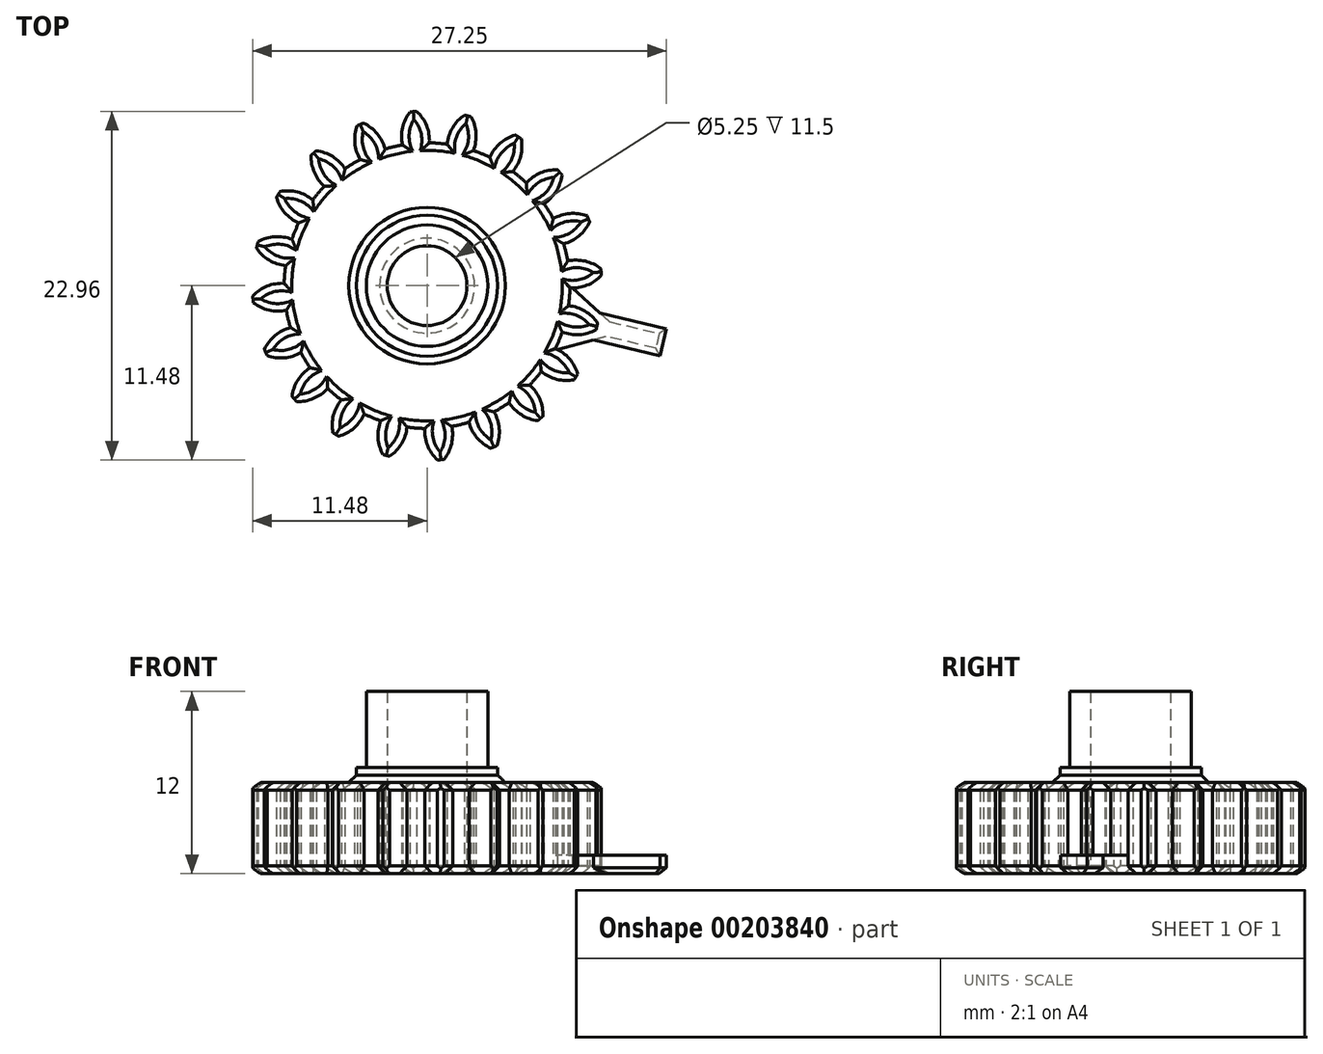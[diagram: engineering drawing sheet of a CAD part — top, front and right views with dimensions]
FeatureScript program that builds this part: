
annotation { "Feature Type Name" : "Feature", "Feature Type Description" : "" }
export const myFeature = defineFeature(function(context is Context, id is Id, definition is map)
    precondition{}
    {
        {
            assignVariable(context, id + "F0", {"name" : "GearDepth", "anyValue" : 6});
        }
        {
            var Q0;
            Q0=qCreatedBy(makeId("Top.planeOp"),FACE);
            var sketch = newSketch(context, id + "F1", { "sketchPlane" : qUnion([Q0])});
            skCircle(sketch, "E0", {"center": v(0, 0) * mm, "radius": 9.4 * mm});
            skCircle(sketch, "E1", {"center": v(0, 0) * mm, "radius": 10.45 * mm, "construction": true});
            skCircle(sketch, "E2", {"center": v(0, 0) * mm, "radius": 11.5 * mm, "construction": true});
            skLineSegment(sketch, "E3", {"start": v(0, 0) * mm, "end": v(0, 17.6) * mm, "construction": true});
            skLineSegment(sketch, "E4", {"start": v(0, 0) * mm, "end": v(-1.42, 18) * mm, "construction": true});
            skLineSegment(sketch, "E5", {"start": v(0, 10.45) * mm, "end": v(-10.54, 10.45) * mm, "construction": true});
            skLineSegment(sketch, "E6", {"start": v(0, 10.45) * mm, "end": v(-10.3, 6.7) * mm, "construction": true});
            skCircle(sketch, "E7", {"center": v(0, 10.45) * mm, "radius": 2.61 * mm, "construction": true});
            skCircle(sketch, "E8", {"center": v(-2.46, 9.56) * mm, "radius": 2.61 * mm, "construction": true});
            skArc(sketch, "E9", {"start": v(-4.91, 10.45) * mm, "mid": v(-4.92, 10.42) * mm, "end": v(-4.94, 10.39) * mm});
            skArc(sketch, "E10.trimOffspring", {"start": v(0.15, 9.4) * mm, "mid": v(-0.03, 10.54) * mm, "end": v(-0.68, 11.48) * mm});
            skArc(sketch, "E11.MirrorCS", {"start": v(-1.62, 9.27) * mm, "mid": v(-1.62, 10.41) * mm, "end": v(-1.12, 11.45) * mm});
            skLineSegment(sketch, "E12", {"start": v(-1.12, 11.45) * mm, "end": v(-0.68, 11.48) * mm});
            skArc(sketch, "E13.1.0", {"start": v(-2.76, 9) * mm, "mid": v(-3.29, 10.01) * mm, "end": v(-4.2, 10.7) * mm});
            skLineSegment(sketch, "E13.1.1", {"start": v(-4.6, 10.54) * mm, "end": v(-4.2, 10.7) * mm});
            skArc(sketch, "E13.1.2", {"start": v(-4.4, 8.31) * mm, "mid": v(-4.76, 9.4) * mm, "end": v(-4.6, 10.54) * mm});
            skArc(sketch, "E13.2.0", {"start": v(-5.4, 7.7) * mm, "mid": v(-6.22, 8.5) * mm, "end": v(-7.3, 8.89) * mm});
            skLineSegment(sketch, "E13.2.1", {"start": v(-7.64, 8.6) * mm, "end": v(-7.3, 8.89) * mm});
            skArc(sketch, "E13.2.2", {"start": v(-6.76, 6.54) * mm, "mid": v(-7.43, 7.47) * mm, "end": v(-7.64, 8.6) * mm});
            skArc(sketch, "E13.3.0", {"start": v(-7.52, 5.65) * mm, "mid": v(-8.54, 6.17) * mm, "end": v(-9.69, 6.2) * mm});
            skLineSegment(sketch, "E13.3.1", {"start": v(-9.92, 5.82) * mm, "end": v(-9.69, 6.2) * mm});
            skArc(sketch, "E13.3.2", {"start": v(-8.45, 4.13) * mm, "mid": v(-9.37, 4.81) * mm, "end": v(-9.92, 5.82) * mm});
            skArc(sketch, "E13.4.0", {"start": v(-8.9, 3.05) * mm, "mid": v(-10.03, 3.23) * mm, "end": v(-11.13, 2.9) * mm});
            skLineSegment(sketch, "E13.4.1", {"start": v(-11.23, 2.47) * mm, "end": v(-11.13, 2.9) * mm});
            skArc(sketch, "E13.4.2", {"start": v(-9.32, 1.32) * mm, "mid": v(-10.4, 1.68) * mm, "end": v(-11.23, 2.47) * mm});
            skArc(sketch, "E13.5.0", {"start": v(-9.4, 0.15) * mm, "mid": v(-10.54, -0.03) * mm, "end": v(-11.48, -0.68) * mm});
            skLineSegment(sketch, "E13.5.1", {"start": v(-11.45, -1.12) * mm, "end": v(-11.48, -0.68) * mm});
            skArc(sketch, "E13.5.2", {"start": v(-9.27, -1.62) * mm, "mid": v(-10.41, -1.62) * mm, "end": v(-11.45, -1.12) * mm});
            skArc(sketch, "E13.6.0", {"start": v(-9, -2.76) * mm, "mid": v(-10.01, -3.29) * mm, "end": v(-10.7, -4.2) * mm});
            skLineSegment(sketch, "E13.6.1", {"start": v(-10.54, -4.6) * mm, "end": v(-10.7, -4.2) * mm});
            skArc(sketch, "E13.6.2", {"start": v(-8.31, -4.4) * mm, "mid": v(-9.4, -4.76) * mm, "end": v(-10.54, -4.6) * mm});
            skArc(sketch, "E13.7.0", {"start": v(-7.7, -5.4) * mm, "mid": v(-8.5, -6.22) * mm, "end": v(-8.89, -7.3) * mm});
            skLineSegment(sketch, "E13.7.1", {"start": v(-8.6, -7.64) * mm, "end": v(-8.89, -7.3) * mm});
            skArc(sketch, "E13.7.2", {"start": v(-6.54, -6.76) * mm, "mid": v(-7.47, -7.43) * mm, "end": v(-8.6, -7.64) * mm});
            skArc(sketch, "E13.8.0", {"start": v(-5.65, -7.52) * mm, "mid": v(-6.17, -8.54) * mm, "end": v(-6.2, -9.69) * mm});
            skLineSegment(sketch, "E13.8.1", {"start": v(-5.82, -9.92) * mm, "end": v(-6.2, -9.69) * mm});
            skArc(sketch, "E13.8.2", {"start": v(-4.13, -8.45) * mm, "mid": v(-4.81, -9.37) * mm, "end": v(-5.82, -9.92) * mm});
            skArc(sketch, "E13.9.0", {"start": v(-3.05, -8.9) * mm, "mid": v(-3.23, -10.03) * mm, "end": v(-2.9, -11.13) * mm});
            skLineSegment(sketch, "E13.9.1", {"start": v(-2.47, -11.23) * mm, "end": v(-2.9, -11.13) * mm});
            skArc(sketch, "E13.9.2", {"start": v(-1.32, -9.32) * mm, "mid": v(-1.68, -10.4) * mm, "end": v(-2.47, -11.23) * mm});
            skArc(sketch, "E13.10.0", {"start": v(-0.15, -9.4) * mm, "mid": v(0.03, -10.54) * mm, "end": v(0.68, -11.48) * mm});
            skLineSegment(sketch, "E13.10.1", {"start": v(1.12, -11.45) * mm, "end": v(0.68, -11.48) * mm});
            skArc(sketch, "E13.10.2", {"start": v(1.62, -9.27) * mm, "mid": v(1.62, -10.41) * mm, "end": v(1.12, -11.45) * mm});
            skArc(sketch, "E13.11.0", {"start": v(2.76, -9) * mm, "mid": v(3.29, -10.01) * mm, "end": v(4.2, -10.7) * mm});
            skLineSegment(sketch, "E13.11.1", {"start": v(4.6, -10.54) * mm, "end": v(4.2, -10.7) * mm});
            skArc(sketch, "E13.11.2", {"start": v(4.4, -8.31) * mm, "mid": v(4.76, -9.4) * mm, "end": v(4.6, -10.54) * mm});
            skArc(sketch, "E13.12.0", {"start": v(5.4, -7.7) * mm, "mid": v(6.22, -8.5) * mm, "end": v(7.3, -8.89) * mm});
            skLineSegment(sketch, "E13.12.1", {"start": v(7.64, -8.6) * mm, "end": v(7.3, -8.89) * mm});
            skArc(sketch, "E13.12.2", {"start": v(6.76, -6.54) * mm, "mid": v(7.43, -7.47) * mm, "end": v(7.64, -8.6) * mm});
            skArc(sketch, "E13.13.0", {"start": v(7.52, -5.65) * mm, "mid": v(8.54, -6.17) * mm, "end": v(9.69, -6.2) * mm});
            skLineSegment(sketch, "E13.13.1", {"start": v(9.92, -5.82) * mm, "end": v(9.69, -6.2) * mm});
            skArc(sketch, "E13.13.2", {"start": v(8.45, -4.13) * mm, "mid": v(9.37, -4.81) * mm, "end": v(9.92, -5.82) * mm});
            skArc(sketch, "E13.14.0", {"start": v(8.9, -3.05) * mm, "mid": v(10.03, -3.23) * mm, "end": v(11.13, -2.9) * mm});
            skLineSegment(sketch, "E13.14.1", {"start": v(11.23, -2.47) * mm, "end": v(11.13, -2.9) * mm});
            skArc(sketch, "E13.14.2", {"start": v(9.32, -1.32) * mm, "mid": v(10.4, -1.68) * mm, "end": v(11.23, -2.47) * mm});
            skArc(sketch, "E13.15.0", {"start": v(9.4, -0.15) * mm, "mid": v(10.54, 0.03) * mm, "end": v(11.48, 0.68) * mm});
            skLineSegment(sketch, "E13.15.1", {"start": v(11.45, 1.12) * mm, "end": v(11.48, 0.68) * mm});
            skArc(sketch, "E13.15.2", {"start": v(9.27, 1.62) * mm, "mid": v(10.41, 1.62) * mm, "end": v(11.45, 1.12) * mm});
            skArc(sketch, "E13.16.0", {"start": v(9, 2.76) * mm, "mid": v(10.01, 3.29) * mm, "end": v(10.7, 4.2) * mm});
            skLineSegment(sketch, "E13.16.1", {"start": v(10.54, 4.6) * mm, "end": v(10.7, 4.2) * mm});
            skArc(sketch, "E13.16.2", {"start": v(8.31, 4.4) * mm, "mid": v(9.4, 4.76) * mm, "end": v(10.54, 4.6) * mm});
            skArc(sketch, "E13.17.0", {"start": v(7.7, 5.4) * mm, "mid": v(8.5, 6.22) * mm, "end": v(8.89, 7.3) * mm});
            skLineSegment(sketch, "E13.17.1", {"start": v(8.6, 7.64) * mm, "end": v(8.89, 7.3) * mm});
            skArc(sketch, "E13.17.2", {"start": v(6.54, 6.76) * mm, "mid": v(7.47, 7.43) * mm, "end": v(8.6, 7.64) * mm});
            skArc(sketch, "E13.18.0", {"start": v(5.65, 7.52) * mm, "mid": v(6.17, 8.54) * mm, "end": v(6.2, 9.69) * mm});
            skLineSegment(sketch, "E13.18.1", {"start": v(5.82, 9.92) * mm, "end": v(6.2, 9.69) * mm});
            skArc(sketch, "E13.18.2", {"start": v(4.13, 8.45) * mm, "mid": v(4.81, 9.37) * mm, "end": v(5.82, 9.92) * mm});
            skArc(sketch, "E13.19.0", {"start": v(3.05, 8.9) * mm, "mid": v(3.23, 10.03) * mm, "end": v(2.9, 11.13) * mm});
            skLineSegment(sketch, "E13.19.1", {"start": v(2.47, 11.23) * mm, "end": v(2.9, 11.13) * mm});
            skArc(sketch, "E13.19.2", {"start": v(1.32, 9.32) * mm, "mid": v(1.68, 10.4) * mm, "end": v(2.47, 11.23) * mm});
            skSolve(sketch);
        }
        {
            var Q0;
            {var subQ0=sQuery(id+"F1.wireOp",EDGE,"E10.trimOffspring");Q0=makeQuery(id+"F1.imprint","IMPRINT",FACE,{"disambiguationData":[TD([[makeQuery(id+"F1.imprint","IMPRINT",EDGE,{"derivedFrom":subQ0}),1.0]])]});}
            var Q1;
            {var subQ0=sQuery(id+"F1.wireOp",EDGE,"E0");var subQ1=makeQuery(id+"F1.imprint","INTERSECT",VERTEX,{"derivedFrom":[subQ0,sQuery(id+"F1.wireOp",EDGE,"E10.trimOffspring")]});Q1=makeQuery(id+"F1.imprint","IMPRINT",FACE,{"disambiguationData":[TD([[makeQuery(id+"F1.imprint","IMPRINT",EDGE,{"disambiguationData":[TD([[subQ1,-1.0]])],"derivedFrom":subQ0}),1.0]])]});}
            var Q2;
            {var subQ0=sQuery(id+"F1.wireOp",EDGE,"E13.1.0");Q2=makeQuery(id+"F1.imprint","IMPRINT",FACE,{"disambiguationData":[TD([[makeQuery(id+"F1.imprint","IMPRINT",EDGE,{"derivedFrom":subQ0}),1.0]])]});}
            var Q3;
            {var subQ0=sQuery(id+"F1.wireOp",EDGE,"E13.2.0");Q3=makeQuery(id+"F1.imprint","IMPRINT",FACE,{"disambiguationData":[TD([[makeQuery(id+"F1.imprint","IMPRINT",EDGE,{"derivedFrom":subQ0}),1.0]])]});}
            var Q4;
            {var subQ0=sQuery(id+"F1.wireOp",EDGE,"E13.3.0");Q4=makeQuery(id+"F1.imprint","IMPRINT",FACE,{"disambiguationData":[TD([[makeQuery(id+"F1.imprint","IMPRINT",EDGE,{"derivedFrom":subQ0}),1.0]])]});}
            var Q5;
            {var subQ0=sQuery(id+"F1.wireOp",EDGE,"E13.4.0");Q5=makeQuery(id+"F1.imprint","IMPRINT",FACE,{"disambiguationData":[TD([[makeQuery(id+"F1.imprint","IMPRINT",EDGE,{"derivedFrom":subQ0}),1.0]])]});}
            var Q6;
            {var subQ0=sQuery(id+"F1.wireOp",EDGE,"E13.5.0");Q6=makeQuery(id+"F1.imprint","IMPRINT",FACE,{"disambiguationData":[TD([[makeQuery(id+"F1.imprint","IMPRINT",EDGE,{"derivedFrom":subQ0}),1.0]])]});}
            var Q7;
            {var subQ0=sQuery(id+"F1.wireOp",EDGE,"E13.6.0");Q7=makeQuery(id+"F1.imprint","IMPRINT",FACE,{"disambiguationData":[TD([[makeQuery(id+"F1.imprint","IMPRINT",EDGE,{"derivedFrom":subQ0}),1.0]])]});}
            var Q8;
            {var subQ0=sQuery(id+"F1.wireOp",EDGE,"E13.7.0");Q8=makeQuery(id+"F1.imprint","IMPRINT",FACE,{"disambiguationData":[TD([[makeQuery(id+"F1.imprint","IMPRINT",EDGE,{"derivedFrom":subQ0}),1.0]])]});}
            var Q9;
            {var subQ0=sQuery(id+"F1.wireOp",EDGE,"E13.8.0");Q9=makeQuery(id+"F1.imprint","IMPRINT",FACE,{"disambiguationData":[TD([[makeQuery(id+"F1.imprint","IMPRINT",EDGE,{"derivedFrom":subQ0}),1.0]])]});}
            var Q10;
            {var subQ0=sQuery(id+"F1.wireOp",EDGE,"E13.9.0");Q10=makeQuery(id+"F1.imprint","IMPRINT",FACE,{"disambiguationData":[TD([[makeQuery(id+"F1.imprint","IMPRINT",EDGE,{"derivedFrom":subQ0}),1.0]])]});}
            var Q11;
            {var subQ0=sQuery(id+"F1.wireOp",EDGE,"E13.10.0");Q11=makeQuery(id+"F1.imprint","IMPRINT",FACE,{"disambiguationData":[TD([[makeQuery(id+"F1.imprint","IMPRINT",EDGE,{"derivedFrom":subQ0}),1.0]])]});}
            var Q12;
            {var subQ0=sQuery(id+"F1.wireOp",EDGE,"E13.11.0");Q12=makeQuery(id+"F1.imprint","IMPRINT",FACE,{"disambiguationData":[TD([[makeQuery(id+"F1.imprint","IMPRINT",EDGE,{"derivedFrom":subQ0}),1.0]])]});}
            var Q13;
            {var subQ0=sQuery(id+"F1.wireOp",EDGE,"E13.12.0");Q13=makeQuery(id+"F1.imprint","IMPRINT",FACE,{"disambiguationData":[TD([[makeQuery(id+"F1.imprint","IMPRINT",EDGE,{"derivedFrom":subQ0}),1.0]])]});}
            var Q14;
            {var subQ0=sQuery(id+"F1.wireOp",EDGE,"E13.13.0");Q14=makeQuery(id+"F1.imprint","IMPRINT",FACE,{"disambiguationData":[TD([[makeQuery(id+"F1.imprint","IMPRINT",EDGE,{"derivedFrom":subQ0}),1.0]])]});}
            var Q15;
            {var subQ0=sQuery(id+"F1.wireOp",EDGE,"E13.14.0");Q15=makeQuery(id+"F1.imprint","IMPRINT",FACE,{"disambiguationData":[TD([[makeQuery(id+"F1.imprint","IMPRINT",EDGE,{"derivedFrom":subQ0}),1.0]])]});}
            var Q16;
            {var subQ0=sQuery(id+"F1.wireOp",EDGE,"E13.15.0");Q16=makeQuery(id+"F1.imprint","IMPRINT",FACE,{"disambiguationData":[TD([[makeQuery(id+"F1.imprint","IMPRINT",EDGE,{"derivedFrom":subQ0}),1.0]])]});}
            var Q17;
            {var subQ0=sQuery(id+"F1.wireOp",EDGE,"E13.16.0");Q17=makeQuery(id+"F1.imprint","IMPRINT",FACE,{"disambiguationData":[TD([[makeQuery(id+"F1.imprint","IMPRINT",EDGE,{"derivedFrom":subQ0}),1.0]])]});}
            var Q18;
            {var subQ0=sQuery(id+"F1.wireOp",EDGE,"E13.17.0");Q18=makeQuery(id+"F1.imprint","IMPRINT",FACE,{"disambiguationData":[TD([[makeQuery(id+"F1.imprint","IMPRINT",EDGE,{"derivedFrom":subQ0}),1.0]])]});}
            var Q19;
            {var subQ0=sQuery(id+"F1.wireOp",EDGE,"E13.18.0");Q19=makeQuery(id+"F1.imprint","IMPRINT",FACE,{"disambiguationData":[TD([[makeQuery(id+"F1.imprint","IMPRINT",EDGE,{"derivedFrom":subQ0}),1.0]])]});}
            var Q20;
            {var subQ0=sQuery(id+"F1.wireOp",EDGE,"E13.19.0");Q20=makeQuery(id+"F1.imprint","IMPRINT",FACE,{"disambiguationData":[TD([[makeQuery(id+"F1.imprint","IMPRINT",EDGE,{"derivedFrom":subQ0}),1.0]])]});}
            var Q21;
            Q21=sQuery(id+"F1.wireOp",EDGE,"E0");
            var Q22;
            Q22=sQuery(id+"F1.wireOp",EDGE,"E10.trimOffspring");
            var Q23;
            Q23=sQuery(id+"F1.wireOp",EDGE,"E12");
            var Q24;
            Q24=sQuery(id+"F1.wireOp",EDGE,"E11.MirrorCS");
            extrude(context, id + "F2", {"entities" : qUnion([Q0, Q1, Q2, Q3, Q4, Q5, Q6, Q7, Q8, Q9, Q10, Q11, Q12, Q13, Q14, Q15, Q16, Q17, Q18, Q19, Q20]), "surfaceEntities" : qUnion([Q21, Q22, Q23, Q24]), "depth" : (getVariable(context, 'GearDepth')) * mm});
        }
        {
            var Q0;
            Q0=makeQuery(id+"F2.opExtrude","CAP_FACE",FACE,{"disambiguationData":[OSD([sQuery(id+"F1.wireOp",EDGE,"E0"),sQuery(id+"F1.wireOp",EDGE,"E10.trimOffspring"),sQuery(id+"F1.wireOp",EDGE,"E11.MirrorCS"),sQuery(id+"F1.wireOp",EDGE,"E12"),sQuery(id+"F1.wireOp",EDGE,"E13.1.0"),sQuery(id+"F1.wireOp",EDGE,"E13.1.1"),sQuery(id+"F1.wireOp",EDGE,"E13.1.2"),sQuery(id+"F1.wireOp",EDGE,"E13.2.0"),sQuery(id+"F1.wireOp",EDGE,"E13.2.1"),sQuery(id+"F1.wireOp",EDGE,"E13.2.2"),sQuery(id+"F1.wireOp",EDGE,"E13.3.0"),sQuery(id+"F1.wireOp",EDGE,"E13.3.1"),sQuery(id+"F1.wireOp",EDGE,"E13.3.2"),sQuery(id+"F1.wireOp",EDGE,"E13.4.0"),sQuery(id+"F1.wireOp",EDGE,"E13.4.1"),sQuery(id+"F1.wireOp",EDGE,"E13.4.2"),sQuery(id+"F1.wireOp",EDGE,"E13.5.0"),sQuery(id+"F1.wireOp",EDGE,"E13.5.1"),sQuery(id+"F1.wireOp",EDGE,"E13.5.2"),sQuery(id+"F1.wireOp",EDGE,"E13.6.0"),sQuery(id+"F1.wireOp",EDGE,"E13.6.1"),sQuery(id+"F1.wireOp",EDGE,"E13.6.2"),sQuery(id+"F1.wireOp",EDGE,"E13.7.0"),sQuery(id+"F1.wireOp",EDGE,"E13.7.1"),sQuery(id+"F1.wireOp",EDGE,"E13.7.2"),sQuery(id+"F1.wireOp",EDGE,"E13.8.0"),sQuery(id+"F1.wireOp",EDGE,"E13.8.1"),sQuery(id+"F1.wireOp",EDGE,"E13.8.2"),sQuery(id+"F1.wireOp",EDGE,"E13.9.0"),sQuery(id+"F1.wireOp",EDGE,"E13.9.1"),sQuery(id+"F1.wireOp",EDGE,"E13.9.2"),sQuery(id+"F1.wireOp",EDGE,"E13.10.0"),sQuery(id+"F1.wireOp",EDGE,"E13.10.1"),sQuery(id+"F1.wireOp",EDGE,"E13.10.2"),sQuery(id+"F1.wireOp",EDGE,"E13.11.0"),sQuery(id+"F1.wireOp",EDGE,"E13.11.1"),sQuery(id+"F1.wireOp",EDGE,"E13.11.2"),sQuery(id+"F1.wireOp",EDGE,"E13.12.0"),sQuery(id+"F1.wireOp",EDGE,"E13.12.1"),sQuery(id+"F1.wireOp",EDGE,"E13.12.2"),sQuery(id+"F1.wireOp",EDGE,"E13.13.0"),sQuery(id+"F1.wireOp",EDGE,"E13.13.1"),sQuery(id+"F1.wireOp",EDGE,"E13.13.2"),sQuery(id+"F1.wireOp",EDGE,"E13.14.0"),sQuery(id+"F1.wireOp",EDGE,"E13.14.1"),sQuery(id+"F1.wireOp",EDGE,"E13.14.2"),sQuery(id+"F1.wireOp",EDGE,"E13.15.0"),sQuery(id+"F1.wireOp",EDGE,"E13.15.1"),sQuery(id+"F1.wireOp",EDGE,"E13.15.2"),sQuery(id+"F1.wireOp",EDGE,"E13.16.0"),sQuery(id+"F1.wireOp",EDGE,"E13.16.1"),sQuery(id+"F1.wireOp",EDGE,"E13.16.2"),sQuery(id+"F1.wireOp",EDGE,"E13.17.0"),sQuery(id+"F1.wireOp",EDGE,"E13.17.1"),sQuery(id+"F1.wireOp",EDGE,"E13.17.2"),sQuery(id+"F1.wireOp",EDGE,"E13.18.0"),sQuery(id+"F1.wireOp",EDGE,"E13.18.1"),sQuery(id+"F1.wireOp",EDGE,"E13.18.2"),sQuery(id+"F1.wireOp",EDGE,"E13.19.0"),sQuery(id+"F1.wireOp",EDGE,"E13.19.1"),sQuery(id+"F1.wireOp",EDGE,"E13.19.2")])],"isStart":true});
            var sketch = newSketch(context, id + "F3", { "sketchPlane" : qUnion([Q0])});
            skCircle(sketch, "E14", {"center": v(0, 0) * mm, "radius": 2.62 * mm});
            skSolve(sketch);
        }
        {
            var Q0;
            Q0=makeQuery(id+"F3.imprint","IMPRINT",FACE,{"disambiguationData":[TD([[makeQuery(id+"F3.imprint","IMPRINT",EDGE,{"derivedFrom":sQuery(id+"F3.wireOp",EDGE,"E14")}),1.0]])]});
            extrude(context, id + "F4", {"entities" : qUnion([Q0]), "operationType" : NewBodyOperationType.REMOVE, "endBound" : BoundingType.UP_TO_NEXT, "oppositeDirection" : true, "depth" : 25 * mm});
        }
        {
            var Q0;
            Q0=makeQuery(id+"F2.opExtrude","CAP_FACE",FACE,{"disambiguationData":[OSD([sQuery(id+"F1.wireOp",EDGE,"E0"),sQuery(id+"F1.wireOp",EDGE,"E10.trimOffspring"),sQuery(id+"F1.wireOp",EDGE,"E11.MirrorCS"),sQuery(id+"F1.wireOp",EDGE,"E12"),sQuery(id+"F1.wireOp",EDGE,"E13.1.0"),sQuery(id+"F1.wireOp",EDGE,"E13.1.1"),sQuery(id+"F1.wireOp",EDGE,"E13.1.2"),sQuery(id+"F1.wireOp",EDGE,"E13.2.0"),sQuery(id+"F1.wireOp",EDGE,"E13.2.1"),sQuery(id+"F1.wireOp",EDGE,"E13.2.2"),sQuery(id+"F1.wireOp",EDGE,"E13.3.0"),sQuery(id+"F1.wireOp",EDGE,"E13.3.1"),sQuery(id+"F1.wireOp",EDGE,"E13.3.2"),sQuery(id+"F1.wireOp",EDGE,"E13.4.0"),sQuery(id+"F1.wireOp",EDGE,"E13.4.1"),sQuery(id+"F1.wireOp",EDGE,"E13.4.2"),sQuery(id+"F1.wireOp",EDGE,"E13.5.0"),sQuery(id+"F1.wireOp",EDGE,"E13.5.1"),sQuery(id+"F1.wireOp",EDGE,"E13.5.2"),sQuery(id+"F1.wireOp",EDGE,"E13.6.0"),sQuery(id+"F1.wireOp",EDGE,"E13.6.1"),sQuery(id+"F1.wireOp",EDGE,"E13.6.2"),sQuery(id+"F1.wireOp",EDGE,"E13.7.0"),sQuery(id+"F1.wireOp",EDGE,"E13.7.1"),sQuery(id+"F1.wireOp",EDGE,"E13.7.2"),sQuery(id+"F1.wireOp",EDGE,"E13.8.0"),sQuery(id+"F1.wireOp",EDGE,"E13.8.1"),sQuery(id+"F1.wireOp",EDGE,"E13.8.2"),sQuery(id+"F1.wireOp",EDGE,"E13.9.0"),sQuery(id+"F1.wireOp",EDGE,"E13.9.1"),sQuery(id+"F1.wireOp",EDGE,"E13.9.2"),sQuery(id+"F1.wireOp",EDGE,"E13.10.0"),sQuery(id+"F1.wireOp",EDGE,"E13.10.1"),sQuery(id+"F1.wireOp",EDGE,"E13.10.2"),sQuery(id+"F1.wireOp",EDGE,"E13.11.0"),sQuery(id+"F1.wireOp",EDGE,"E13.11.1"),sQuery(id+"F1.wireOp",EDGE,"E13.11.2"),sQuery(id+"F1.wireOp",EDGE,"E13.12.0"),sQuery(id+"F1.wireOp",EDGE,"E13.12.1"),sQuery(id+"F1.wireOp",EDGE,"E13.12.2"),sQuery(id+"F1.wireOp",EDGE,"E13.13.0"),sQuery(id+"F1.wireOp",EDGE,"E13.13.1"),sQuery(id+"F1.wireOp",EDGE,"E13.13.2"),sQuery(id+"F1.wireOp",EDGE,"E13.14.0"),sQuery(id+"F1.wireOp",EDGE,"E13.14.1"),sQuery(id+"F1.wireOp",EDGE,"E13.14.2"),sQuery(id+"F1.wireOp",EDGE,"E13.15.0"),sQuery(id+"F1.wireOp",EDGE,"E13.15.1"),sQuery(id+"F1.wireOp",EDGE,"E13.15.2"),sQuery(id+"F1.wireOp",EDGE,"E13.16.0"),sQuery(id+"F1.wireOp",EDGE,"E13.16.1"),sQuery(id+"F1.wireOp",EDGE,"E13.16.2"),sQuery(id+"F1.wireOp",EDGE,"E13.17.0"),sQuery(id+"F1.wireOp",EDGE,"E13.17.1"),sQuery(id+"F1.wireOp",EDGE,"E13.17.2"),sQuery(id+"F1.wireOp",EDGE,"E13.18.0"),sQuery(id+"F1.wireOp",EDGE,"E13.18.1"),sQuery(id+"F1.wireOp",EDGE,"E13.18.2"),sQuery(id+"F1.wireOp",EDGE,"E13.19.0"),sQuery(id+"F1.wireOp",EDGE,"E13.19.1"),sQuery(id+"F1.wireOp",EDGE,"E13.19.2")])],"isStart":true});
            var sketch = newSketch(context, id + "F5", { "sketchPlane" : qUnion([Q0])});
            skCircle(sketch, "E15", {"center": v(0, 0) * mm, "radius": 4.65 * mm});
            skSolve(sketch);
        }
        {
            var Q0;
            Q0=makeQuery(id+"F5.imprint","IMPRINT",FACE,{"disambiguationData":[TD([[makeQuery(id+"F5.imprint","IMPRINT",EDGE,{"derivedFrom":sQuery(id+"F5.wireOp",EDGE,"E15")}),1.0]])]});
            extrude(context, id + "F6", {"entities" : qUnion([Q0]), "operationType" : NewBodyOperationType.ADD, "oppositeDirection" : true, "depth" : 7 * mm});
        }
        {
            var Q0;
            Q0=makeQuery(id+"F6.opExtrude","CAP_FACE",FACE,{"disambiguationData":[OSD([sQuery(id+"F3.wireOp",EDGE,"E14"),sQuery(id+"F5.wireOp",EDGE,"E15")])],"isStart":false});
            var sketch = newSketch(context, id + "F7", { "sketchPlane" : qUnion([Q0])});
            skCircle(sketch, "E16", {"center": v(0, 0) * mm, "radius": 4 * mm});
            skSolve(sketch);
        }
        {
            var Q0;
            Q0=makeQuery(id+"F7.imprint","IMPRINT",FACE,{"disambiguationData":[TD([[makeQuery(id+"F7.imprint","IMPRINT",EDGE,{"derivedFrom":sQuery(id+"F7.wireOp",EDGE,"E16")}),1.0]])]});
            extrude(context, id + "F8", {"entities" : qUnion([Q0]), "operationType" : NewBodyOperationType.ADD, "depth" : (1.8 + 1 + 2.2) * mm});
        }
        {
            var Q0;
            Q0=makeQuery(id+"F2.opExtrude","CAP_FACE",FACE,{"disambiguationData":[OSD([sQuery(id+"F1.wireOp",EDGE,"E0"),sQuery(id+"F1.wireOp",EDGE,"E10.trimOffspring"),sQuery(id+"F1.wireOp",EDGE,"E11.MirrorCS"),sQuery(id+"F1.wireOp",EDGE,"E12"),sQuery(id+"F1.wireOp",EDGE,"E13.1.0"),sQuery(id+"F1.wireOp",EDGE,"E13.1.1"),sQuery(id+"F1.wireOp",EDGE,"E13.1.2"),sQuery(id+"F1.wireOp",EDGE,"E13.2.0"),sQuery(id+"F1.wireOp",EDGE,"E13.2.1"),sQuery(id+"F1.wireOp",EDGE,"E13.2.2"),sQuery(id+"F1.wireOp",EDGE,"E13.3.0"),sQuery(id+"F1.wireOp",EDGE,"E13.3.1"),sQuery(id+"F1.wireOp",EDGE,"E13.3.2"),sQuery(id+"F1.wireOp",EDGE,"E13.4.0"),sQuery(id+"F1.wireOp",EDGE,"E13.4.1"),sQuery(id+"F1.wireOp",EDGE,"E13.4.2"),sQuery(id+"F1.wireOp",EDGE,"E13.5.0"),sQuery(id+"F1.wireOp",EDGE,"E13.5.1"),sQuery(id+"F1.wireOp",EDGE,"E13.5.2"),sQuery(id+"F1.wireOp",EDGE,"E13.6.0"),sQuery(id+"F1.wireOp",EDGE,"E13.6.1"),sQuery(id+"F1.wireOp",EDGE,"E13.6.2"),sQuery(id+"F1.wireOp",EDGE,"E13.7.0"),sQuery(id+"F1.wireOp",EDGE,"E13.7.1"),sQuery(id+"F1.wireOp",EDGE,"E13.7.2"),sQuery(id+"F1.wireOp",EDGE,"E13.8.0"),sQuery(id+"F1.wireOp",EDGE,"E13.8.1"),sQuery(id+"F1.wireOp",EDGE,"E13.8.2"),sQuery(id+"F1.wireOp",EDGE,"E13.9.0"),sQuery(id+"F1.wireOp",EDGE,"E13.9.1"),sQuery(id+"F1.wireOp",EDGE,"E13.9.2"),sQuery(id+"F1.wireOp",EDGE,"E13.10.0"),sQuery(id+"F1.wireOp",EDGE,"E13.10.1"),sQuery(id+"F1.wireOp",EDGE,"E13.10.2"),sQuery(id+"F1.wireOp",EDGE,"E13.11.0"),sQuery(id+"F1.wireOp",EDGE,"E13.11.1"),sQuery(id+"F1.wireOp",EDGE,"E13.11.2"),sQuery(id+"F1.wireOp",EDGE,"E13.12.0"),sQuery(id+"F1.wireOp",EDGE,"E13.12.1"),sQuery(id+"F1.wireOp",EDGE,"E13.12.2"),sQuery(id+"F1.wireOp",EDGE,"E13.13.0"),sQuery(id+"F1.wireOp",EDGE,"E13.13.1"),sQuery(id+"F1.wireOp",EDGE,"E13.13.2"),sQuery(id+"F1.wireOp",EDGE,"E13.14.0"),sQuery(id+"F1.wireOp",EDGE,"E13.14.1"),sQuery(id+"F1.wireOp",EDGE,"E13.14.2"),sQuery(id+"F1.wireOp",EDGE,"E13.15.0"),sQuery(id+"F1.wireOp",EDGE,"E13.15.1"),sQuery(id+"F1.wireOp",EDGE,"E13.15.2"),sQuery(id+"F1.wireOp",EDGE,"E13.16.0"),sQuery(id+"F1.wireOp",EDGE,"E13.16.1"),sQuery(id+"F1.wireOp",EDGE,"E13.16.2"),sQuery(id+"F1.wireOp",EDGE,"E13.17.0"),sQuery(id+"F1.wireOp",EDGE,"E13.17.1"),sQuery(id+"F1.wireOp",EDGE,"E13.17.2"),sQuery(id+"F1.wireOp",EDGE,"E13.18.0"),sQuery(id+"F1.wireOp",EDGE,"E13.18.1"),sQuery(id+"F1.wireOp",EDGE,"E13.18.2"),sQuery(id+"F1.wireOp",EDGE,"E13.19.0"),sQuery(id+"F1.wireOp",EDGE,"E13.19.1"),sQuery(id+"F1.wireOp",EDGE,"E13.19.2")])],"isStart":true});
            var Q1;
            Q1=makeQuery(id+"F2.opExtrude","CAP_FACE",FACE,{"disambiguationData":[OSD([sQuery(id+"F1.wireOp",EDGE,"E0"),sQuery(id+"F1.wireOp",EDGE,"E10.trimOffspring"),sQuery(id+"F1.wireOp",EDGE,"E11.MirrorCS"),sQuery(id+"F1.wireOp",EDGE,"E12"),sQuery(id+"F1.wireOp",EDGE,"E13.1.0"),sQuery(id+"F1.wireOp",EDGE,"E13.1.1"),sQuery(id+"F1.wireOp",EDGE,"E13.1.2"),sQuery(id+"F1.wireOp",EDGE,"E13.2.0"),sQuery(id+"F1.wireOp",EDGE,"E13.2.1"),sQuery(id+"F1.wireOp",EDGE,"E13.2.2"),sQuery(id+"F1.wireOp",EDGE,"E13.3.0"),sQuery(id+"F1.wireOp",EDGE,"E13.3.1"),sQuery(id+"F1.wireOp",EDGE,"E13.3.2"),sQuery(id+"F1.wireOp",EDGE,"E13.4.0"),sQuery(id+"F1.wireOp",EDGE,"E13.4.1"),sQuery(id+"F1.wireOp",EDGE,"E13.4.2"),sQuery(id+"F1.wireOp",EDGE,"E13.5.0"),sQuery(id+"F1.wireOp",EDGE,"E13.5.1"),sQuery(id+"F1.wireOp",EDGE,"E13.5.2"),sQuery(id+"F1.wireOp",EDGE,"E13.6.0"),sQuery(id+"F1.wireOp",EDGE,"E13.6.1"),sQuery(id+"F1.wireOp",EDGE,"E13.6.2"),sQuery(id+"F1.wireOp",EDGE,"E13.7.0"),sQuery(id+"F1.wireOp",EDGE,"E13.7.1"),sQuery(id+"F1.wireOp",EDGE,"E13.7.2"),sQuery(id+"F1.wireOp",EDGE,"E13.8.0"),sQuery(id+"F1.wireOp",EDGE,"E13.8.1"),sQuery(id+"F1.wireOp",EDGE,"E13.8.2"),sQuery(id+"F1.wireOp",EDGE,"E13.9.0"),sQuery(id+"F1.wireOp",EDGE,"E13.9.1"),sQuery(id+"F1.wireOp",EDGE,"E13.9.2"),sQuery(id+"F1.wireOp",EDGE,"E13.10.0"),sQuery(id+"F1.wireOp",EDGE,"E13.10.1"),sQuery(id+"F1.wireOp",EDGE,"E13.10.2"),sQuery(id+"F1.wireOp",EDGE,"E13.11.0"),sQuery(id+"F1.wireOp",EDGE,"E13.11.1"),sQuery(id+"F1.wireOp",EDGE,"E13.11.2"),sQuery(id+"F1.wireOp",EDGE,"E13.12.0"),sQuery(id+"F1.wireOp",EDGE,"E13.12.1"),sQuery(id+"F1.wireOp",EDGE,"E13.12.2"),sQuery(id+"F1.wireOp",EDGE,"E13.13.0"),sQuery(id+"F1.wireOp",EDGE,"E13.13.1"),sQuery(id+"F1.wireOp",EDGE,"E13.13.2"),sQuery(id+"F1.wireOp",EDGE,"E13.14.0"),sQuery(id+"F1.wireOp",EDGE,"E13.14.1"),sQuery(id+"F1.wireOp",EDGE,"E13.14.2"),sQuery(id+"F1.wireOp",EDGE,"E13.15.0"),sQuery(id+"F1.wireOp",EDGE,"E13.15.1"),sQuery(id+"F1.wireOp",EDGE,"E13.15.2"),sQuery(id+"F1.wireOp",EDGE,"E13.16.0"),sQuery(id+"F1.wireOp",EDGE,"E13.16.1"),sQuery(id+"F1.wireOp",EDGE,"E13.16.2"),sQuery(id+"F1.wireOp",EDGE,"E13.17.0"),sQuery(id+"F1.wireOp",EDGE,"E13.17.1"),sQuery(id+"F1.wireOp",EDGE,"E13.17.2"),sQuery(id+"F1.wireOp",EDGE,"E13.18.0"),sQuery(id+"F1.wireOp",EDGE,"E13.18.1"),sQuery(id+"F1.wireOp",EDGE,"E13.18.2"),sQuery(id+"F1.wireOp",EDGE,"E13.19.0"),sQuery(id+"F1.wireOp",EDGE,"E13.19.1"),sQuery(id+"F1.wireOp",EDGE,"E13.19.2")])],"isStart":false});
            chamfer(context, id + "F9", {"entities" : qUnion([Q0, Q1]), "width" : 0.5 * mm, "tangentPropagation" : true});
        }
        {
            var Q0;
            Q0=makeQuery(id+"F2.opExtrude","CAP_FACE",FACE,{"disambiguationData":[OSD([sQuery(id+"F1.wireOp",EDGE,"E0"),sQuery(id+"F1.wireOp",EDGE,"E10.trimOffspring"),sQuery(id+"F1.wireOp",EDGE,"E11.MirrorCS"),sQuery(id+"F1.wireOp",EDGE,"E12"),sQuery(id+"F1.wireOp",EDGE,"E13.1.0"),sQuery(id+"F1.wireOp",EDGE,"E13.1.1"),sQuery(id+"F1.wireOp",EDGE,"E13.1.2"),sQuery(id+"F1.wireOp",EDGE,"E13.2.0"),sQuery(id+"F1.wireOp",EDGE,"E13.2.1"),sQuery(id+"F1.wireOp",EDGE,"E13.2.2"),sQuery(id+"F1.wireOp",EDGE,"E13.3.0"),sQuery(id+"F1.wireOp",EDGE,"E13.3.1"),sQuery(id+"F1.wireOp",EDGE,"E13.3.2"),sQuery(id+"F1.wireOp",EDGE,"E13.4.0"),sQuery(id+"F1.wireOp",EDGE,"E13.4.1"),sQuery(id+"F1.wireOp",EDGE,"E13.4.2"),sQuery(id+"F1.wireOp",EDGE,"E13.5.0"),sQuery(id+"F1.wireOp",EDGE,"E13.5.1"),sQuery(id+"F1.wireOp",EDGE,"E13.5.2"),sQuery(id+"F1.wireOp",EDGE,"E13.6.0"),sQuery(id+"F1.wireOp",EDGE,"E13.6.1"),sQuery(id+"F1.wireOp",EDGE,"E13.6.2"),sQuery(id+"F1.wireOp",EDGE,"E13.7.0"),sQuery(id+"F1.wireOp",EDGE,"E13.7.1"),sQuery(id+"F1.wireOp",EDGE,"E13.7.2"),sQuery(id+"F1.wireOp",EDGE,"E13.8.0"),sQuery(id+"F1.wireOp",EDGE,"E13.8.1"),sQuery(id+"F1.wireOp",EDGE,"E13.8.2"),sQuery(id+"F1.wireOp",EDGE,"E13.9.0"),sQuery(id+"F1.wireOp",EDGE,"E13.9.1"),sQuery(id+"F1.wireOp",EDGE,"E13.9.2"),sQuery(id+"F1.wireOp",EDGE,"E13.10.0"),sQuery(id+"F1.wireOp",EDGE,"E13.10.1"),sQuery(id+"F1.wireOp",EDGE,"E13.10.2"),sQuery(id+"F1.wireOp",EDGE,"E13.11.0"),sQuery(id+"F1.wireOp",EDGE,"E13.11.1"),sQuery(id+"F1.wireOp",EDGE,"E13.11.2"),sQuery(id+"F1.wireOp",EDGE,"E13.12.0"),sQuery(id+"F1.wireOp",EDGE,"E13.12.1"),sQuery(id+"F1.wireOp",EDGE,"E13.12.2"),sQuery(id+"F1.wireOp",EDGE,"E13.13.0"),sQuery(id+"F1.wireOp",EDGE,"E13.13.1"),sQuery(id+"F1.wireOp",EDGE,"E13.13.2"),sQuery(id+"F1.wireOp",EDGE,"E13.14.0"),sQuery(id+"F1.wireOp",EDGE,"E13.14.1"),sQuery(id+"F1.wireOp",EDGE,"E13.14.2"),sQuery(id+"F1.wireOp",EDGE,"E13.15.0"),sQuery(id+"F1.wireOp",EDGE,"E13.15.1"),sQuery(id+"F1.wireOp",EDGE,"E13.15.2"),sQuery(id+"F1.wireOp",EDGE,"E13.16.0"),sQuery(id+"F1.wireOp",EDGE,"E13.16.1"),sQuery(id+"F1.wireOp",EDGE,"E13.16.2"),sQuery(id+"F1.wireOp",EDGE,"E13.17.0"),sQuery(id+"F1.wireOp",EDGE,"E13.17.1"),sQuery(id+"F1.wireOp",EDGE,"E13.17.2"),sQuery(id+"F1.wireOp",EDGE,"E13.18.0"),sQuery(id+"F1.wireOp",EDGE,"E13.18.1"),sQuery(id+"F1.wireOp",EDGE,"E13.18.2"),sQuery(id+"F1.wireOp",EDGE,"E13.19.0"),sQuery(id+"F1.wireOp",EDGE,"E13.19.1"),sQuery(id+"F1.wireOp",EDGE,"E13.19.2")])],"isStart":true});
            var sketch = newSketch(context, id + "F10", { "sketchPlane" : qUnion([Q0])});
            skLineSegment(sketch, "E17.bottom", {"start": v(10.97, 3.56) * mm, "end": v(15.35, 4.61) * mm});
            skLineSegment(sketch, "E17.top", {"start": v(11.4, 1.8) * mm, "end": v(15.77, 2.86) * mm});
            skLineSegment(sketch, "E17.right", {"start": v(15.35, 4.61) * mm, "end": v(15.77, 2.86) * mm});
            skPoint(sketch, "E18", {"position": v(11.18, 2.68) * mm});
            skLineSegment(sketch, "E19", {"start": v(10.97, 3.56) * mm, "end": v(7.72, 4.44) * mm});
            skLineSegment(sketch, "E20", {"start": v(11.4, 1.8) * mm, "end": v(8.9, -0.45) * mm});
            skLineSegment(sketch, "E21", {"start": v(8.9, -0.45) * mm, "end": v(7.72, 4.44) * mm});
            skLineSegment(sketch, "E22", {"start": v(10.97, 3.56) * mm, "end": v(11.4, 1.8) * mm, "construction": true});
            skSolve(sketch);
        }
        {
            var Q0;
            Q0=makeQuery(id+"F10.imprint","IMPRINT",FACE,{"disambiguationData":[TD([[makeQuery(id+"F10.imprint","IMPRINT",EDGE,{"derivedFrom":sQuery(id+"F10.wireOp",EDGE,"E17.bottom")}),-1.0]])]});
            extrude(context, id + "F11", {"entities" : qUnion([Q0]), "operationType" : NewBodyOperationType.ADD, "oppositeDirection" : true, "depth" : 1.2 * mm});
        }
        {
            var Q0;
            Q0=makeQuery(id+"F11.opExtrude","CAP_EDGE",EDGE,{"disambiguationData":[OSD([sQuery(id+"F10.wireOp",EDGE,"E17.bottom")])],"isStart":true});
            var Q1;
            Q1=makeQuery(id+"F11.opExtrude","CAP_EDGE",EDGE,{"disambiguationData":[OSD([sQuery(id+"F10.wireOp",EDGE,"E17.right")])],"isStart":true});
            var Q2;
            Q2=makeQuery(id+"F11.opExtrude","CAP_EDGE",EDGE,{"disambiguationData":[OSD([sQuery(id+"F10.wireOp",EDGE,"E17.top")])],"isStart":true});
            chamfer(context, id + "F12", {"entities" : qUnion([Q0, Q1, Q2]), "width" : 0.4 * mm, "tangentPropagation" : true});
        }
    });
